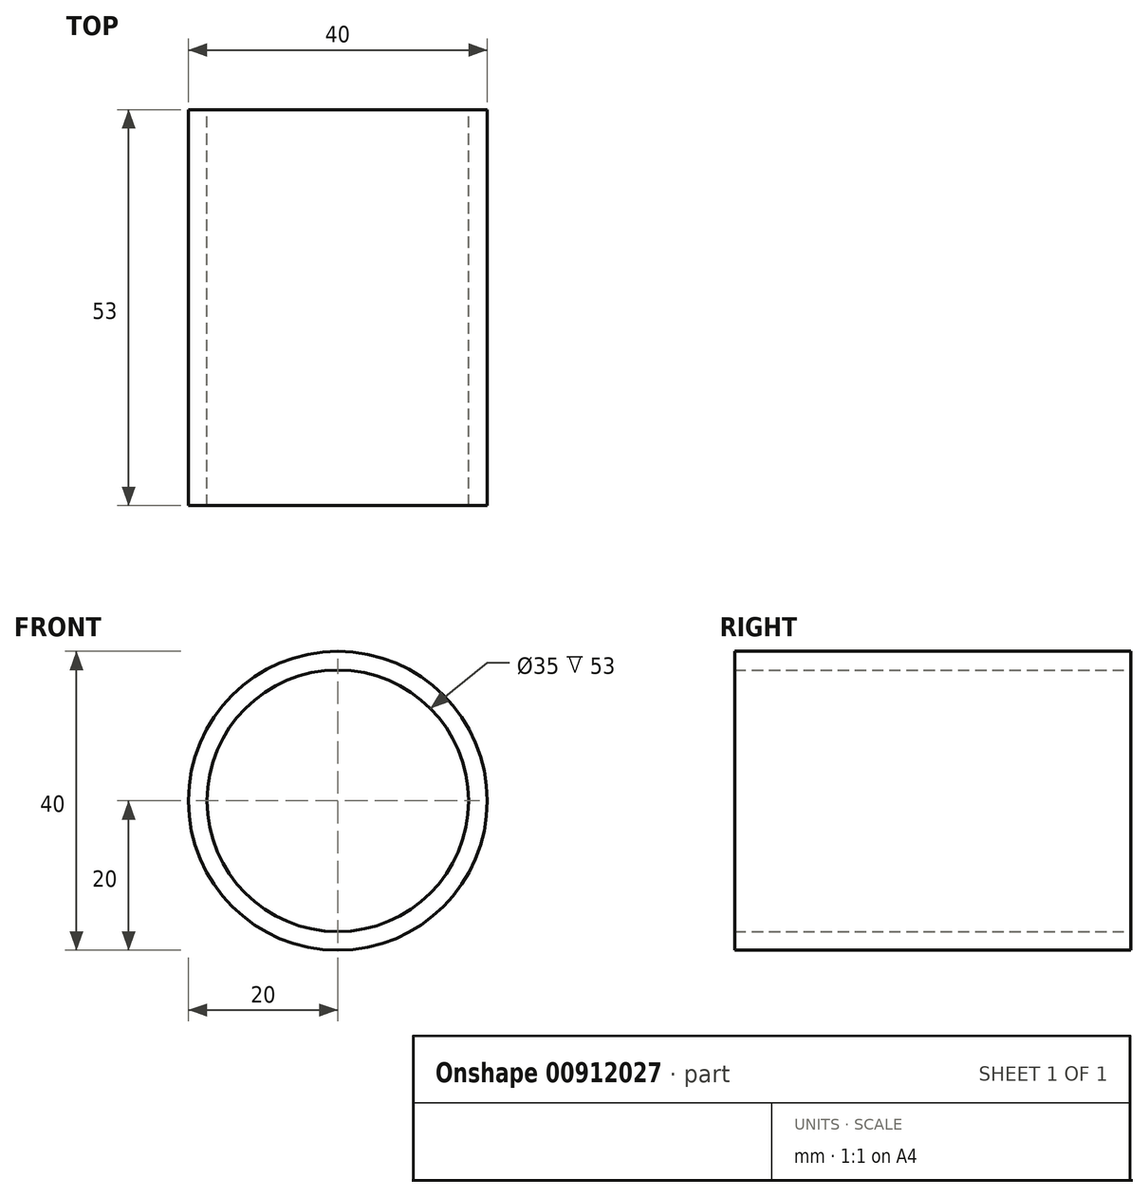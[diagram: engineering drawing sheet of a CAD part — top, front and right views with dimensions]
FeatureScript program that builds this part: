
annotation { "Feature Type Name" : "Feature", "Feature Type Description" : "" }
export const myFeature = defineFeature(function(context is Context, id is Id, definition is map)
    precondition{}
    {
        {
            var Q0;
            Q0=qCreatedBy(makeId("Front.planeOp"),FACE);
            var sketch = newSketch(context, id + "F0", { "sketchPlane" : qUnion([Q0])});
            skCircle(sketch, "E0", {"center": v(0, 0) * mm, "radius": 17.5 * mm});
            skCircle(sketch, "E1", {"center": v(0, 0) * mm, "radius": 20 * mm});
            skSolve(sketch);
        }
        {
            var Q0;
            Q0 = qSketchRegion(id + "F0", true);
            extrude(context, id + "F1", {"entities" : qUnion([Q0]), "depth" : 53 * mm, "offsetDistance" : 25 * mm});
        }
    });
